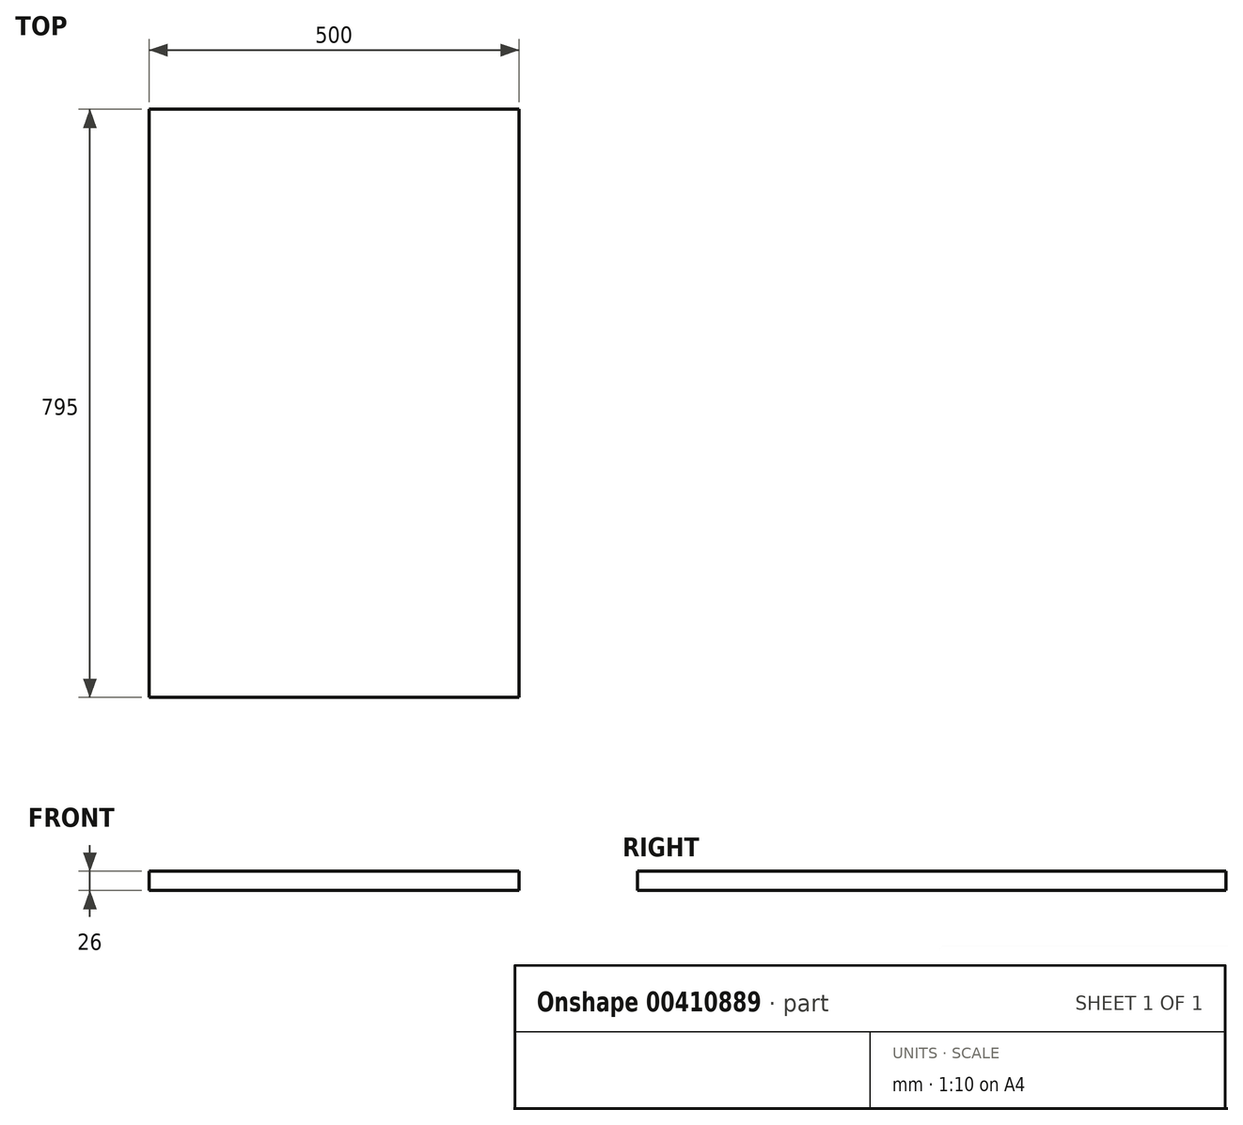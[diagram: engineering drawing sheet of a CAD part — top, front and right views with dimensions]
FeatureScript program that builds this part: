
annotation { "Feature Type Name" : "Feature", "Feature Type Description" : "" }
export const myFeature = defineFeature(function(context is Context, id is Id, definition is map)
    precondition{}
    {
        {
            var Q0;
            Q0=qCreatedBy(makeId("Top.planeOp"),FACE);
            var sketch = newSketch(context, id + "F0", { "sketchPlane" : qUnion([Q0])});
            skLineSegment(sketch, "E0.bottom", {"start": v(250, -397.5) * mm, "end": v(-250, -397.5) * mm});
            skLineSegment(sketch, "E0.top", {"start": v(250, 397.5) * mm, "end": v(-250, 397.5) * mm});
            skLineSegment(sketch, "E0.left", {"start": v(250, -397.5) * mm, "end": v(250, 397.5) * mm});
            skLineSegment(sketch, "E0.right", {"start": v(-250, -397.5) * mm, "end": v(-250, 397.5) * mm});
            skPoint(sketch, "E0.middle", {"position": v(0, 0) * mm});
            skSolve(sketch);
        }
        {
            var Q0;
            Q0=makeQuery(id+"F0.imprint","IMPRINT",FACE,{"disambiguationData":[TD([[makeQuery(id+"F0.imprint","IMPRINT",EDGE,{"derivedFrom":sQuery(id+"F0.wireOp",EDGE,"E0.bottom")}),-1.0]])]});
            extrude(context, id + "F1", {"entities" : qUnion([Q0]), "depth" : 26 * mm});
        }
    });
